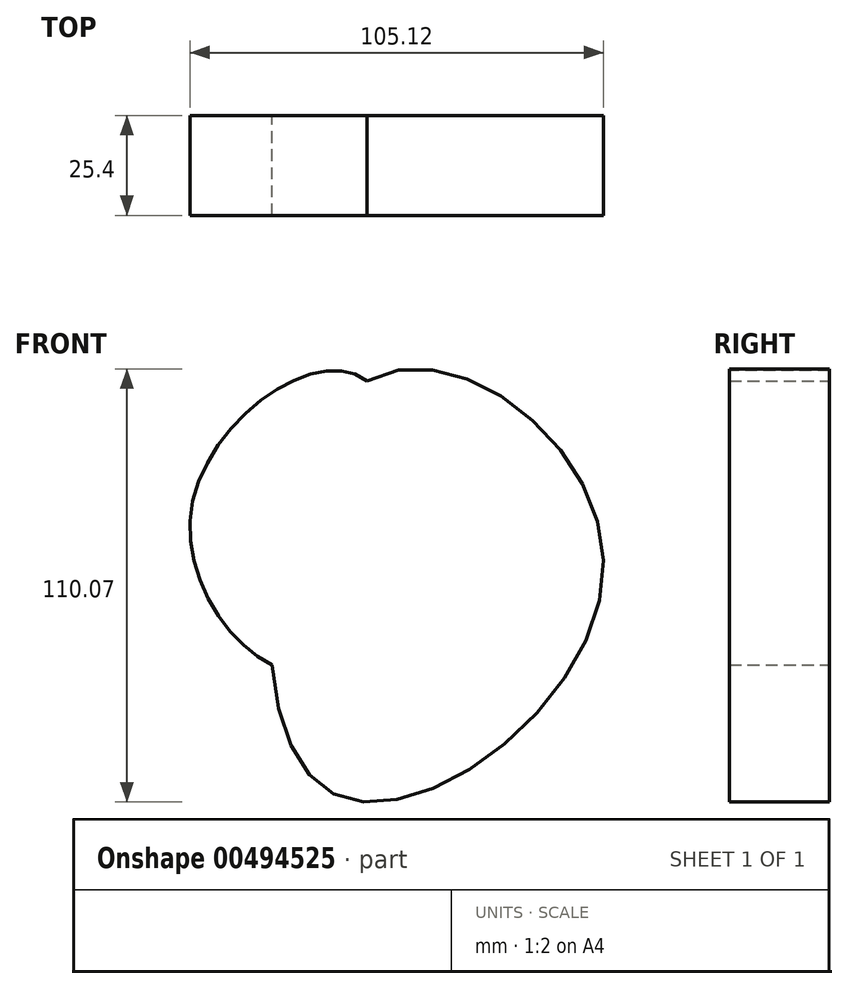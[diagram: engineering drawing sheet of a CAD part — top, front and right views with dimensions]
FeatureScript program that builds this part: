
annotation { "Feature Type Name" : "Feature", "Feature Type Description" : "" }
export const myFeature = defineFeature(function(context is Context, id is Id, definition is map)
    precondition{}
    {
        {
            var Q0;
            Q0=qCreatedBy(makeId("Front.planeOp"),FACE);
            var sketch = newSketch(context, id + "F0", { "sketchPlane" : qUnion([Q0])});
            skFitSpline(sketch, "E0", {"points": [v(10.47, 72.96) * mm, v(70.5, 24.39) * mm, v(0, -30.79) * mm, v(10.47, 72.96) * mm]});
            skFitSpline(sketch, "E1", {"points": [v(-34.36, 39.47) * mm, v(10.47, 72.96) * mm, v(0, 0) * mm, v(-34.36, 39.47) * mm]});
            skSolve(sketch);
        }
        {
            var Q0;
            Q0 = qSketchRegion(id + "F0", true);
            extrude(context, id + "F1", {"entities" : qUnion([Q0]), "depth" : 25.4 * mm});
        }
    });
